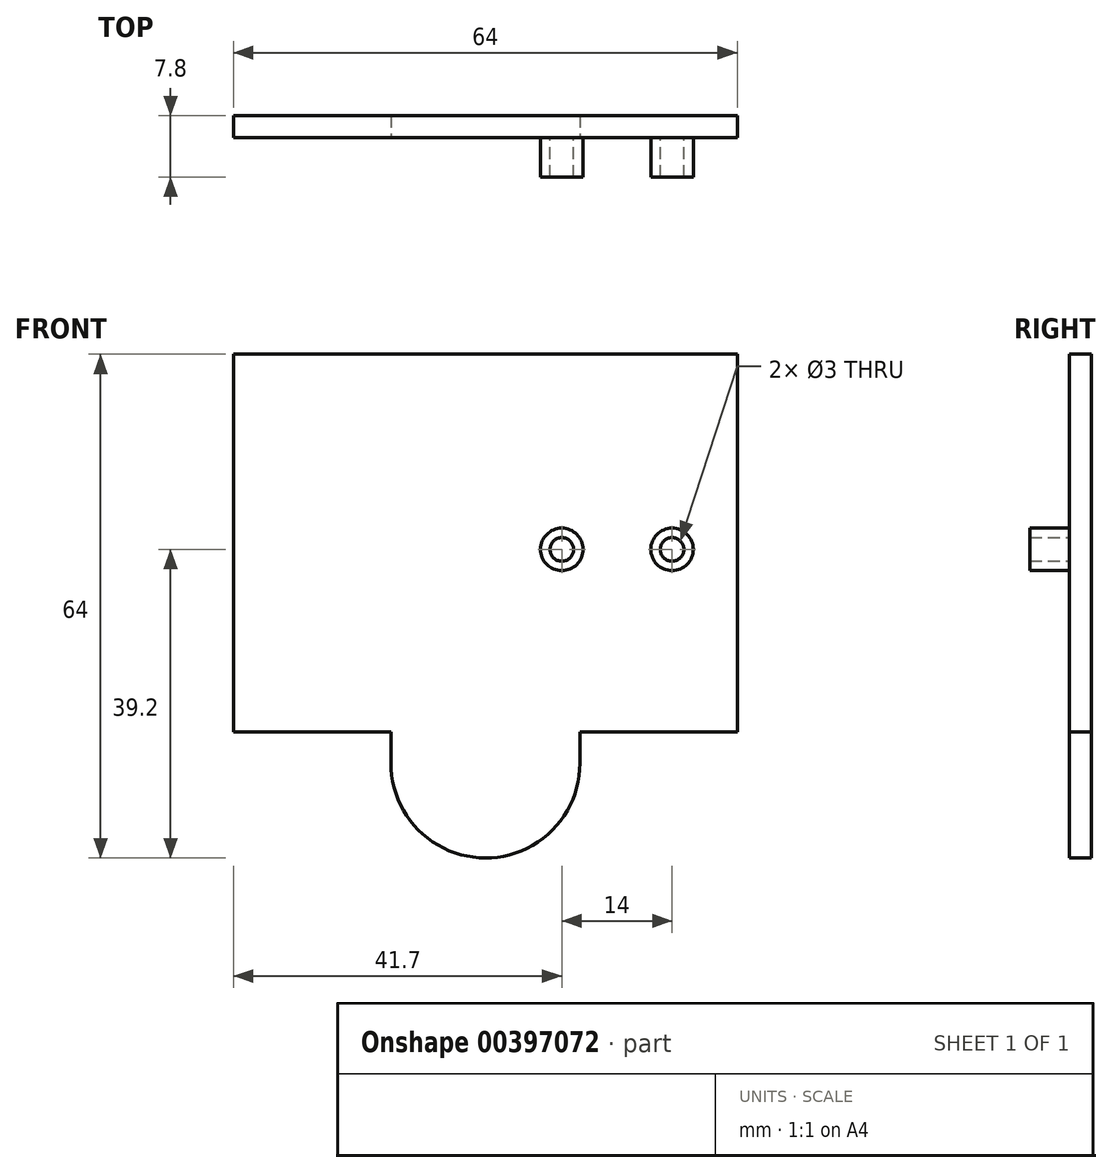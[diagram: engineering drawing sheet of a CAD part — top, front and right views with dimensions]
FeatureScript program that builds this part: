
annotation { "Feature Type Name" : "Feature", "Feature Type Description" : "" }
export const myFeature = defineFeature(function(context is Context, id is Id, definition is map)
    precondition{}
    {
        {
            var Q0;
            Q0=qCreatedBy(makeId("Front.planeOp"),FACE);
            var sketch = newSketch(context, id + "F0", { "sketchPlane" : qUnion([Q0])});
            skLineSegment(sketch, "E0.bottom", {"start": v(32, -24) * mm, "end": v(12, -24) * mm});
            skLineSegment(sketch, "E0.top", {"start": v(32, 24) * mm, "end": v(-32, 24) * mm});
            skLineSegment(sketch, "E0.left", {"start": v(32, -24) * mm, "end": v(32, 24) * mm});
            skLineSegment(sketch, "E0.right", {"start": v(-32, -24) * mm, "end": v(-32, 24) * mm});
            skPoint(sketch, "E0.middle", {"position": v(0, 0) * mm});
            skCircle(sketch, "E1", {"center": v(23.7, -0.8) * mm, "radius": 2.7 * mm});
            skCircle(sketch, "E2", {"center": v(9.7, -0.8) * mm, "radius": 2.7 * mm});
            skCircle(sketch, "E3", {"center": v(23.7, -0.8) * mm, "radius": 1.5 * mm});
            skCircle(sketch, "E4", {"center": v(9.7, -0.8) * mm, "radius": 1.5 * mm});
            skArc(sketch, "E5", {"start": v(-12, -27.9) * mm, "mid": v(-0.03, -40) * mm, "end": v(12, -27.96) * mm});
            skLineSegment(sketch, "E6", {"start": v(12, -28.04) * mm, "end": v(12, -24) * mm});
            skLineSegment(sketch, "E7", {"start": v(-12, -27.9) * mm, "end": v(-12, -24) * mm});
            skLineSegment(sketch, "E8.trimOffspring", {"start": v(-12, -24) * mm, "end": v(-32, -24) * mm});
            skSolve(sketch);
        }
        {
            var Q0;
            Q0=makeQuery(id+"F0.imprint","IMPRINT",FACE,{"disambiguationData":[TD([[makeQuery(id+"F0.imprint","IMPRINT",EDGE,{"derivedFrom":sQuery(id+"F0.wireOp",EDGE,"E1")}),1.0]])]});
            var Q1;
            Q1=makeQuery(id+"F0.imprint","IMPRINT",FACE,{"disambiguationData":[TD([[makeQuery(id+"F0.imprint","IMPRINT",EDGE,{"derivedFrom":sQuery(id+"F0.wireOp",EDGE,"E2")}),1.0]])]});
            extrude(context, id + "F1", {"entities" : qUnion([Q0, Q1]), "depth" : 5 * mm});
        }
        {
            var Q0;
            Q0=qSketchRegion(id+"F0",true);
            var Q1;
            Q1=makeQuery(id+"F0.imprint","IMPRINT",FACE,{"disambiguationData":[TD([[makeQuery(id+"F0.imprint","IMPRINT",EDGE,{"derivedFrom":sQuery(id+"F0.wireOp",EDGE,"E2")}),1.0]])]});
            var Q2;
            Q2=makeQuery(id+"F0.imprint","IMPRINT",FACE,{"disambiguationData":[TD([[makeQuery(id+"F0.imprint","IMPRINT",EDGE,{"derivedFrom":sQuery(id+"F0.wireOp",EDGE,"E4")}),1.0]])]});
            var Q3;
            Q3=makeQuery(id+"F0.imprint","IMPRINT",FACE,{"disambiguationData":[TD([[makeQuery(id+"F0.imprint","IMPRINT",EDGE,{"derivedFrom":sQuery(id+"F0.wireOp",EDGE,"E1")}),1.0]])]});
            var Q4;
            Q4=makeQuery(id+"F0.imprint","IMPRINT",FACE,{"disambiguationData":[TD([[makeQuery(id+"F0.imprint","IMPRINT",EDGE,{"derivedFrom":sQuery(id+"F0.wireOp",EDGE,"E3")}),1.0]])]});
            extrude(context, id + "F2", {"entities" : qUnion([Q0, Q1, Q2, Q3, Q4]), "oppositeDirection" : true, "depth" : 2.8 * mm});
        }
    });
